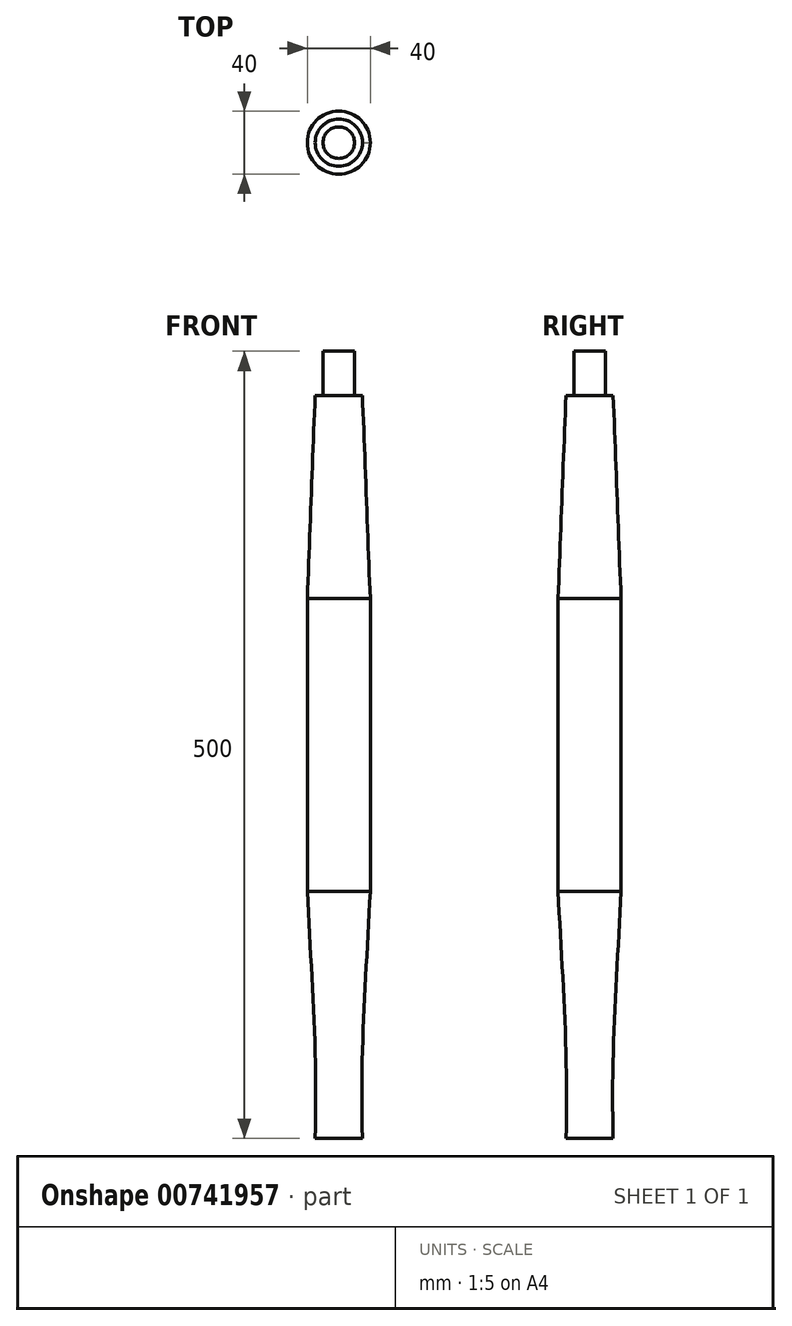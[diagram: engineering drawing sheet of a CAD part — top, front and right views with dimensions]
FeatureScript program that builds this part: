
annotation { "Feature Type Name" : "Feature", "Feature Type Description" : "" }
export const myFeature = defineFeature(function(context is Context, id is Id, definition is map)
    precondition{}
    {
        {
            var Q0;
            Q0=qCreatedBy(makeId("Front.planeOp"),FACE);
            var sketch = newSketch(context, id + "F0", { "sketchPlane" : qUnion([Q0])});
            skLineSegment(sketch, "E0", {"start": v(0, 0) * mm, "end": v(0, 250) * mm});
            skLineSegment(sketch, "E1", {"start": v(20, 92.95) * mm, "end": v(20, 0) * mm});
            skLineSegment(sketch, "E2.MirrorCS", {"start": v(20, -92.95) * mm, "end": v(20, 0) * mm});
            skLineSegment(sketch, "E3.MirrorCS", {"start": v(0, 0) * mm, "end": v(0, -250) * mm});
            skLineSegment(sketch, "E4", {"start": v(15, 222) * mm, "end": v(10, 222) * mm});
            skLineSegment(sketch, "E5", {"start": v(10, 222) * mm, "end": v(10, 250) * mm});
            skLineSegment(sketch, "E6", {"start": v(10, 250) * mm, "end": v(0, 250) * mm});
            skFitSpline(sketch, "E7", {"points": [v(15, 222) * mm, v(20, 92.95) * mm], "startDerivative": vector(5, -122.05) * mm, "endDerivative": vector(5, -122.05) * mm});
            skLineSegment(sketch, "E8", {"start": v(0, -250) * mm, "end": v(15, -250) * mm});
            skFitSpline(sketch, "E9", {"points": [v(15, -250) * mm, v(20, -92.95) * mm], "startDerivative": vector(-4.79, 169.24) * mm, "endDerivative": vector(7.85, 162.62) * mm});
            skSolve(sketch);
        }
        {
            var Q0;
            Q0=makeQuery(id+"F0.imprint","IMPRINT",FACE,{"disambiguationData":[TD([[makeQuery(id+"F0.imprint","IMPRINT",EDGE,{"derivedFrom":sQuery(id+"F0.wireOp",EDGE,"E0")}),-1.0]])]});
            var Q1;
            Q1=makeQuery(id+"F0.imprint","IMPRINT",FACE,{"disambiguationData":[TD([[makeQuery(id+"F0.imprint","IMPRINT",EDGE,{"derivedFrom":sQuery(id+"F0.wireOp",EDGE,"CjWrrxx0-ISEx-yxa1-8jfl-dFYM9Hkqyzem")}),1.0]])]});
            var Q2;
            Q2=sQuery(id+"F0.wireOp",EDGE,"E0");
            revolve(context, id + "F1", {"surfaceOperationType" : NewSurfaceOperationType.NEW, "entities" : qUnion([Q0, Q1]), "axis" : qUnion([Q2]), "revolveType" : RevolveType.FULL, "oppositeDirection" : true});
        }
    });
